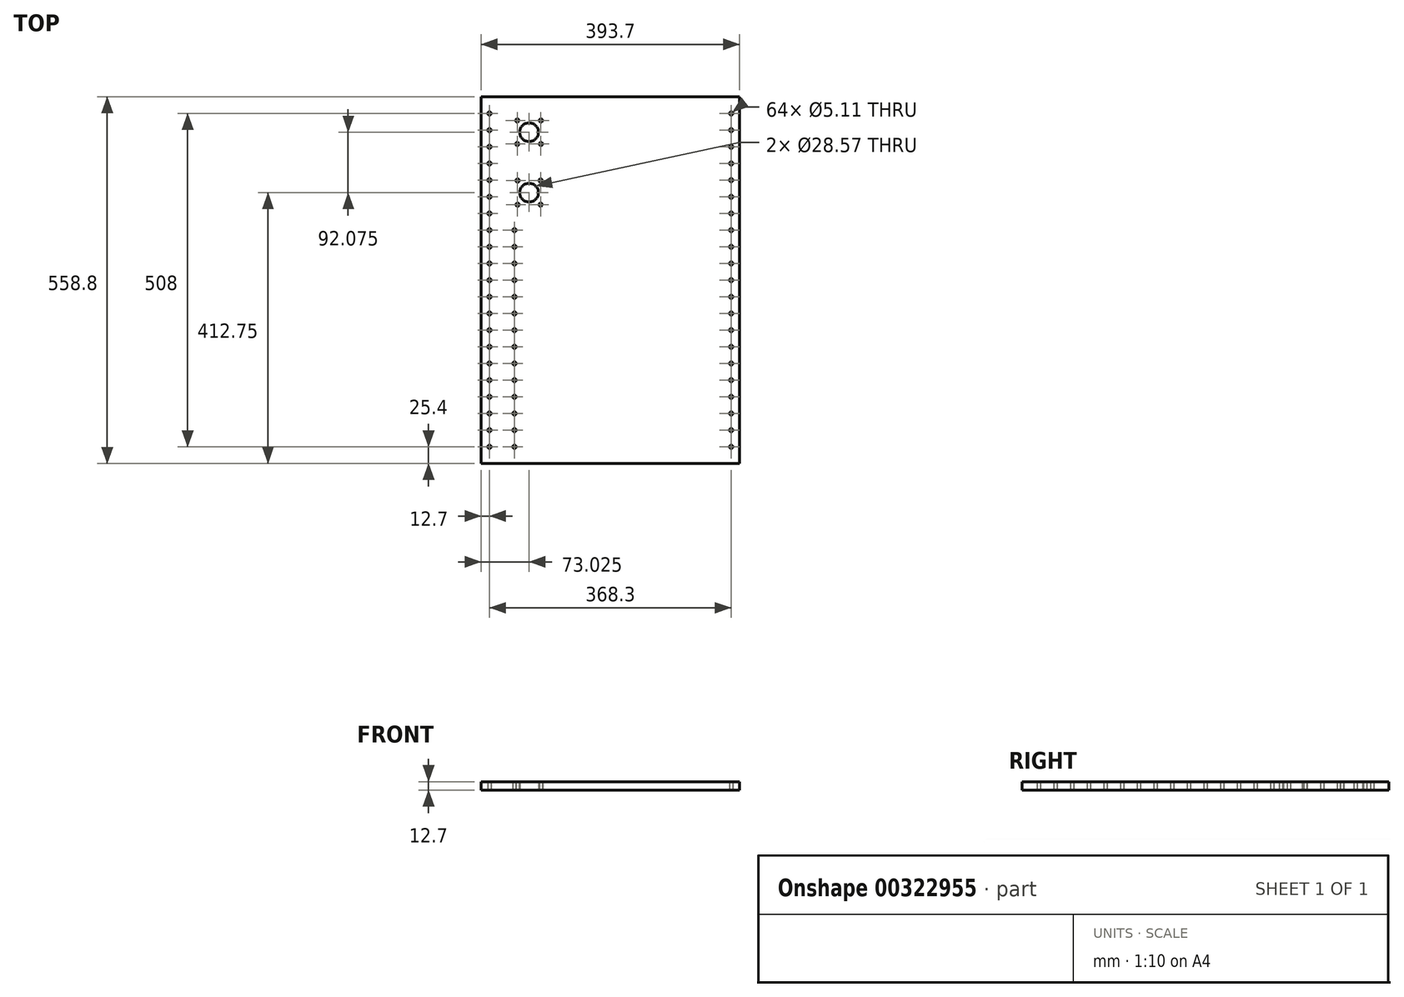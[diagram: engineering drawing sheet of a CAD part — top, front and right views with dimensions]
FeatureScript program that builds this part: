
annotation { "Feature Type Name" : "Feature", "Feature Type Description" : "" }
export const myFeature = defineFeature(function(context is Context, id is Id, definition is map)
    precondition{}
    {
        {
            var Q0;
            Q0=qCreatedBy(makeId("Top.planeOp"),FACE);
            var sketch = newSketch(context, id + "F0", { "sketchPlane" : qUnion([Q0])});
            skLineSegment(sketch, "E0.bottom", {"start": v(196.85, -279.4) * mm, "end": v(-196.85, -279.4) * mm});
            skLineSegment(sketch, "E0.top", {"start": v(196.85, 279.4) * mm, "end": v(-196.85, 279.4) * mm});
            skLineSegment(sketch, "E0.left", {"start": v(196.85, -279.4) * mm, "end": v(196.85, 279.4) * mm});
            skLineSegment(sketch, "E0.right", {"start": v(-196.85, -279.4) * mm, "end": v(-196.85, 279.4) * mm});
            skPoint(sketch, "E0.middle", {"position": v(0, 0) * mm});
            skLineSegment(sketch, "E1.bottom", {"start": v(196.85, 279.4) * mm, "end": v(171.45, 279.4) * mm});
            skLineSegment(sketch, "E1.top", {"start": v(196.85, -279.4) * mm, "end": v(171.45, -279.4) * mm});
            skLineSegment(sketch, "E1.left", {"start": v(196.85, 279.4) * mm, "end": v(196.85, -279.4) * mm});
            skLineSegment(sketch, "E1.right", {"start": v(171.45, 279.4) * mm, "end": v(171.45, -279.4) * mm, "construction": true});
            skLineSegment(sketch, "E2.bottom", {"start": v(-196.85, 279.4) * mm, "end": v(-171.45, 279.4) * mm});
            skLineSegment(sketch, "E2.top", {"start": v(-196.85, -279.4) * mm, "end": v(-171.45, -279.4) * mm});
            skLineSegment(sketch, "E2.left", {"start": v(-196.85, 279.4) * mm, "end": v(-196.85, -279.4) * mm});
            skCircle(sketch, "E3", {"center": v(-123.83, 225.43) * mm, "radius": 41.28 * mm, "construction": true});
            skCircle(sketch, "E4", {"center": v(-123.83, 133.35) * mm, "radius": 38.1 * mm, "construction": true});
            skLineSegment(sketch, "E5", {"start": v(-171.45, 279.4) * mm, "end": v(-171.45, 88.9) * mm, "construction": true});
            skLineSegment(sketch, "E6", {"start": v(-171.45, 88.9) * mm, "end": v(-133.35, 88.9) * mm, "construction": true});
            skLineSegment(sketch, "E7", {"start": v(-133.35, 88.9) * mm, "end": v(-133.35, -279.4) * mm, "construction": true});
            skLineSegment(sketch, "E8", {"start": v(-133.35, -279.4) * mm, "end": v(-158.75, -279.4) * mm});
            skLineSegment(sketch, "E9", {"start": v(-158.75, -279.4) * mm, "end": v(-158.75, 63.5) * mm, "construction": true});
            skLineSegment(sketch, "E10", {"start": v(-158.75, 63.5) * mm, "end": v(-171.45, 63.5) * mm, "construction": true});
            skCircle(sketch, "E11", {"center": v(184.15, 254) * mm, "radius": 2.55 * mm});
            skCircle(sketch, "E12.1.0.0", {"center": v(184.15, 228.6) * mm, "radius": 2.55 * mm});
            skCircle(sketch, "E12.2.0.0", {"center": v(184.15, 203.2) * mm, "radius": 2.55 * mm});
            skCircle(sketch, "E12.3.0.0", {"center": v(184.15, 177.8) * mm, "radius": 2.55 * mm});
            skCircle(sketch, "E12.4.0.0", {"center": v(184.15, 152.4) * mm, "radius": 2.55 * mm});
            skCircle(sketch, "E12.5.0.0", {"center": v(184.15, 127) * mm, "radius": 2.55 * mm});
            skCircle(sketch, "E12.6.0.0", {"center": v(184.15, 101.6) * mm, "radius": 2.55 * mm});
            skCircle(sketch, "E12.7.0.0", {"center": v(184.15, 76.2) * mm, "radius": 2.55 * mm});
            skCircle(sketch, "E12.8.0.0", {"center": v(184.15, 50.8) * mm, "radius": 2.55 * mm});
            skCircle(sketch, "E12.9.0.0", {"center": v(184.15, 25.4) * mm, "radius": 2.55 * mm});
            skCircle(sketch, "E12.10.0.0", {"center": v(184.15, 0) * mm, "radius": 2.55 * mm});
            skCircle(sketch, "E12.11.0.0", {"center": v(184.15, -25.4) * mm, "radius": 2.55 * mm});
            skCircle(sketch, "E12.12.0.0", {"center": v(184.15, -50.8) * mm, "radius": 2.55 * mm});
            skCircle(sketch, "E12.13.0.0", {"center": v(184.15, -76.2) * mm, "radius": 2.55 * mm});
            skCircle(sketch, "E12.14.0.0", {"center": v(184.15, -101.6) * mm, "radius": 2.55 * mm});
            skCircle(sketch, "E12.15.0.0", {"center": v(184.15, -127) * mm, "radius": 2.55 * mm});
            skCircle(sketch, "E12.16.0.0", {"center": v(184.15, -152.4) * mm, "radius": 2.55 * mm});
            skCircle(sketch, "E12.17.0.0", {"center": v(184.15, -177.8) * mm, "radius": 2.55 * mm});
            skCircle(sketch, "E12.18.0.0", {"center": v(184.15, -203.2) * mm, "radius": 2.55 * mm});
            skCircle(sketch, "E12.19.0.0", {"center": v(184.15, -228.6) * mm, "radius": 2.55 * mm});
            skCircle(sketch, "E12.20.0.0", {"center": v(184.15, -254) * mm, "radius": 2.55 * mm});
            skLineSegment(sketch, "E12.direction1", {"start": v(184.15, 254) * mm, "end": v(184.15, 228.6) * mm, "construction": true});
            skCircle(sketch, "E13", {"center": v(-184.15, 254) * mm, "radius": 2.55 * mm});
            skCircle(sketch, "E14.1.0.0", {"center": v(-184.15, 228.6) * mm, "radius": 2.55 * mm});
            skCircle(sketch, "E14.2.0.0", {"center": v(-184.15, 203.2) * mm, "radius": 2.55 * mm});
            skCircle(sketch, "E14.3.0.0", {"center": v(-184.15, 177.8) * mm, "radius": 2.55 * mm});
            skCircle(sketch, "E14.4.0.0", {"center": v(-184.15, 152.4) * mm, "radius": 2.55 * mm});
            skCircle(sketch, "E14.5.0.0", {"center": v(-184.15, 127) * mm, "radius": 2.55 * mm});
            skCircle(sketch, "E14.6.0.0", {"center": v(-184.15, 101.6) * mm, "radius": 2.55 * mm});
            skCircle(sketch, "E14.7.0.0", {"center": v(-184.15, 76.2) * mm, "radius": 2.55 * mm});
            skCircle(sketch, "E14.8.0.0", {"center": v(-184.15, 50.8) * mm, "radius": 2.55 * mm});
            skCircle(sketch, "E14.9.0.0", {"center": v(-184.15, 25.4) * mm, "radius": 2.55 * mm});
            skCircle(sketch, "E14.10.0.0", {"center": v(-184.15, 0) * mm, "radius": 2.55 * mm});
            skCircle(sketch, "E14.11.0.0", {"center": v(-184.15, -25.4) * mm, "radius": 2.55 * mm});
            skCircle(sketch, "E14.12.0.0", {"center": v(-184.15, -50.8) * mm, "radius": 2.55 * mm});
            skCircle(sketch, "E14.13.0.0", {"center": v(-184.15, -76.2) * mm, "radius": 2.55 * mm});
            skCircle(sketch, "E14.14.0.0", {"center": v(-184.15, -101.6) * mm, "radius": 2.55 * mm});
            skCircle(sketch, "E14.15.0.0", {"center": v(-184.15, -127) * mm, "radius": 2.55 * mm});
            skCircle(sketch, "E14.16.0.0", {"center": v(-184.15, -152.4) * mm, "radius": 2.55 * mm});
            skCircle(sketch, "E14.17.0.0", {"center": v(-184.15, -177.8) * mm, "radius": 2.55 * mm});
            skCircle(sketch, "E14.18.0.0", {"center": v(-184.15, -203.2) * mm, "radius": 2.55 * mm});
            skCircle(sketch, "E14.19.0.0", {"center": v(-184.15, -228.6) * mm, "radius": 2.55 * mm});
            skCircle(sketch, "E14.20.0.0", {"center": v(-184.15, -254) * mm, "radius": 2.55 * mm});
            skLineSegment(sketch, "E14.direction1", {"start": v(-184.15, 254) * mm, "end": v(-184.15, 228.6) * mm, "construction": true});
            skCircle(sketch, "E15", {"center": v(-146.05, 76.2) * mm, "radius": 2.55 * mm});
            skCircle(sketch, "E16.1.0.0", {"center": v(-146.05, 50.8) * mm, "radius": 2.55 * mm});
            skCircle(sketch, "E16.2.0.0", {"center": v(-146.05, 25.4) * mm, "radius": 2.55 * mm});
            skCircle(sketch, "E16.3.0.0", {"center": v(-146.05, 0) * mm, "radius": 2.55 * mm});
            skCircle(sketch, "E16.4.0.0", {"center": v(-146.05, -25.4) * mm, "radius": 2.55 * mm});
            skCircle(sketch, "E16.5.0.0", {"center": v(-146.05, -50.8) * mm, "radius": 2.55 * mm});
            skCircle(sketch, "E16.6.0.0", {"center": v(-146.05, -76.2) * mm, "radius": 2.55 * mm});
            skCircle(sketch, "E16.7.0.0", {"center": v(-146.05, -101.6) * mm, "radius": 2.55 * mm});
            skCircle(sketch, "E16.8.0.0", {"center": v(-146.05, -127) * mm, "radius": 2.55 * mm});
            skCircle(sketch, "E16.9.0.0", {"center": v(-146.05, -152.4) * mm, "radius": 2.55 * mm});
            skCircle(sketch, "E16.10.0.0", {"center": v(-146.05, -177.8) * mm, "radius": 2.55 * mm});
            skCircle(sketch, "E16.11.0.0", {"center": v(-146.05, -203.2) * mm, "radius": 2.55 * mm});
            skCircle(sketch, "E16.12.0.0", {"center": v(-146.05, -228.6) * mm, "radius": 2.55 * mm});
            skCircle(sketch, "E16.13.0.0", {"center": v(-146.05, -254) * mm, "radius": 2.55 * mm});
            skLineSegment(sketch, "E16.direction1", {"start": v(-146.05, 76.2) * mm, "end": v(-146.05, 50.8) * mm, "construction": true});
            skCircle(sketch, "E17", {"center": v(-123.83, 225.43) * mm, "radius": 14.29 * mm});
            skCircle(sketch, "E18", {"center": v(-123.83, 133.35) * mm, "radius": 14.29 * mm});
            skLineSegment(sketch, "E19.bottom", {"start": v(-105.76, 207.57) * mm, "end": v(-141.9, 207.57) * mm, "construction": true});
            skLineSegment(sketch, "E19.top", {"start": v(-105.76, 243.28) * mm, "end": v(-141.9, 243.28) * mm, "construction": true});
            skLineSegment(sketch, "E19.left", {"start": v(-105.76, 207.57) * mm, "end": v(-105.76, 243.28) * mm, "construction": true});
            skLineSegment(sketch, "E19.right", {"start": v(-141.9, 207.57) * mm, "end": v(-141.9, 243.28) * mm, "construction": true});
            skLineSegment(sketch, "E20.bottom", {"start": v(-106.3, 114.97) * mm, "end": v(-141.35, 114.97) * mm, "construction": true});
            skLineSegment(sketch, "E20.top", {"start": v(-106.3, 151.73) * mm, "end": v(-141.35, 151.73) * mm, "construction": true});
            skLineSegment(sketch, "E20.left", {"start": v(-106.3, 114.97) * mm, "end": v(-106.3, 151.73) * mm, "construction": true});
            skLineSegment(sketch, "E20.right", {"start": v(-141.35, 114.97) * mm, "end": v(-141.35, 151.73) * mm, "construction": true});
            skCircle(sketch, "E21", {"center": v(-141.9, 243.28) * mm, "radius": 2.55 * mm});
            skCircle(sketch, "E22", {"center": v(-105.76, 243.28) * mm, "radius": 2.55 * mm});
            skCircle(sketch, "E23", {"center": v(-141.9, 207.57) * mm, "radius": 2.55 * mm});
            skCircle(sketch, "E24", {"center": v(-105.76, 207.57) * mm, "radius": 2.55 * mm});
            skCircle(sketch, "E25", {"center": v(-141.35, 151.73) * mm, "radius": 2.55 * mm});
            skCircle(sketch, "E26", {"center": v(-106.3, 151.73) * mm, "radius": 2.55 * mm});
            skCircle(sketch, "E27", {"center": v(-106.3, 114.97) * mm, "radius": 2.55 * mm});
            skCircle(sketch, "E28", {"center": v(-141.35, 114.97) * mm, "radius": 2.55 * mm});
            skSolve(sketch);
        }
        {
            var Q0;
            Q0=makeQuery(id+"F0.imprint","IMPRINT",FACE,{"disambiguationData":[TD([[makeQuery(id+"F0.imprint","IMPRINT",EDGE,{"derivedFrom":sQuery(id+"F0.wireOp",EDGE,"E0.top")}),1.0]])]});
            extrude(context, id + "F1", {"entities" : qUnion([Q0]), "depth" : 12.7 * mm});
        }
    });
